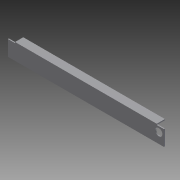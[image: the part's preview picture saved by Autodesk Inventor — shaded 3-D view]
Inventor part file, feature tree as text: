
AUTODESK INVENTOR PART (.ipt)
format: ipt  version: 2012 (Build 160160000, 160)  size: 93,696 bytes
history: native  units: in
note: dims shown in document units (in); Inventor stores cm internally (conversion verified against a paired STEP export)
features: extrude x3, sketch x3
ambient origin geometry x8: Origin, YZ Plane, XZ Plane, XY Plane, X Axis, Y Axis, Z Axis, Center Point
bodies: Solid1 (feature_tree)
feature tree (6):
  extrude  "Extrusion1"  Depth=1.0in
  extrude  "Extrusion2"  Depth=0.125in
  extrude  "Extrusion3"  Depth=20.0in TaperAngle=0.0deg
  sketch  "Sketch1"  dims[d0=2.0in d1=1.0in]
  sketch  "Sketch2"  dims[d2=0.125in d3=0.125in]
  sketch  "Sketch3"  dims[d4=19.0in d5=0.0in d11=20.0in d12=0.0in d13=0.75in d14=0.625in d15=0.875in d16=0.875in d17=0.125in d18=0.0in d19=0.875in]
